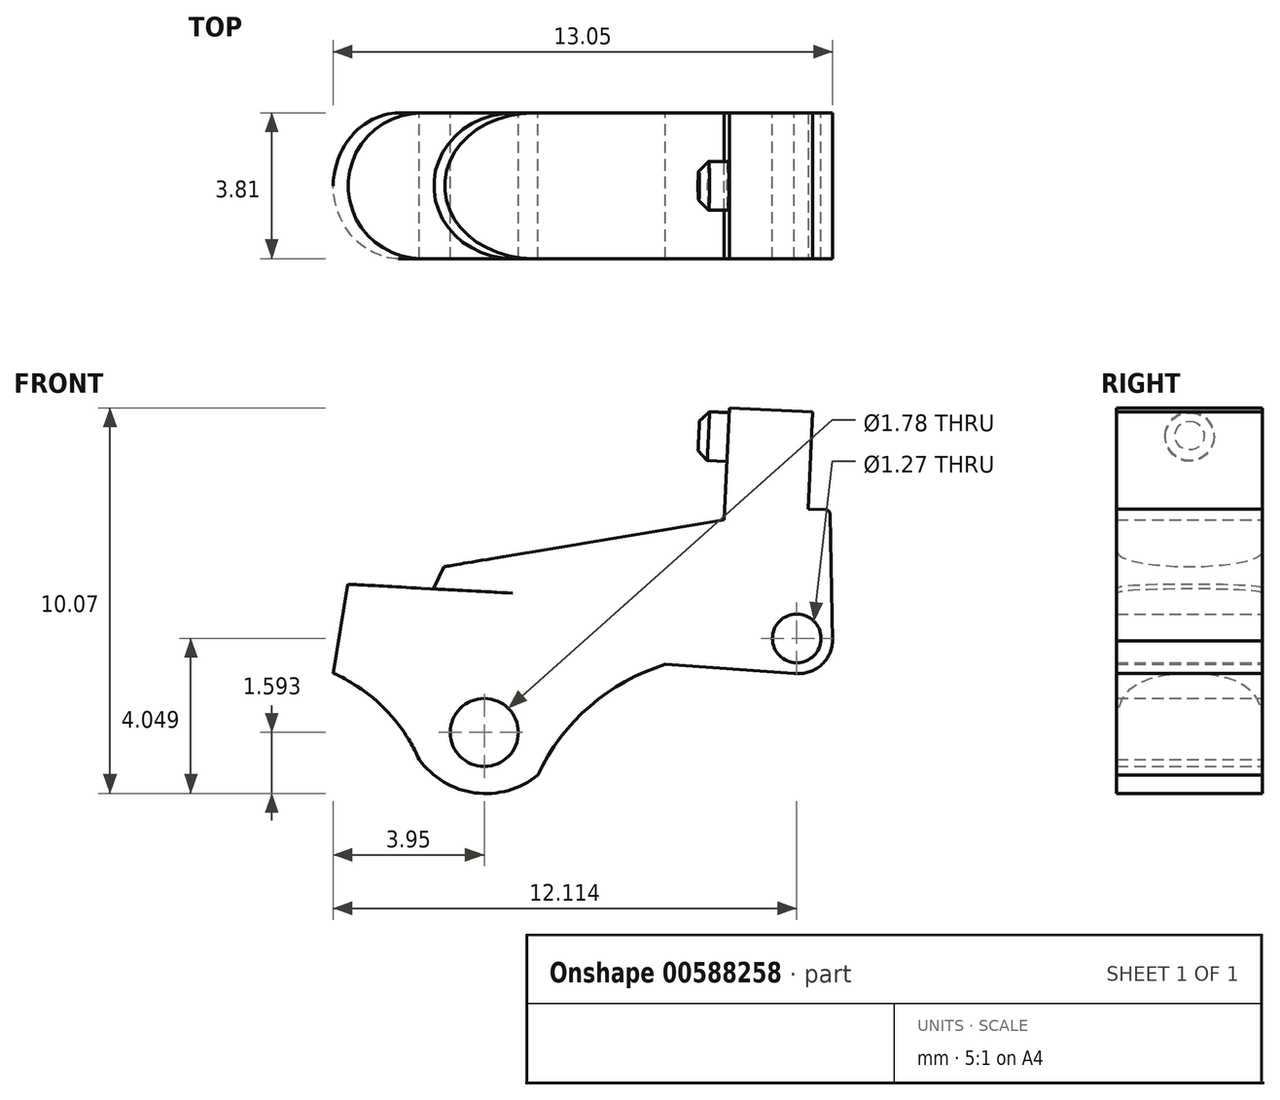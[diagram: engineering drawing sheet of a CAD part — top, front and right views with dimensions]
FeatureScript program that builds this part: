
annotation { "Feature Type Name" : "Feature", "Feature Type Description" : "" }
export const myFeature = defineFeature(function(context is Context, id is Id, definition is map)
    precondition{}
    {
        {
            var Q0;
            Q0=qCreatedBy(makeId("Front.planeOp"),FACE);
            var sketch = newSketch(context, id + "F0", { "sketchPlane" : qUnion([Q0])});
            skPoint(sketch, "E0.endSnap0", {"position": v(-39.55, 26.31) * mm});
            skLineSegment(sketch, "E1", {"start": v(-42.35, 27.7) * mm, "end": v(-42.32, 27.7) * mm});
            skLineSegment(sketch, "E2", {"start": v(-39.7, 29.9) * mm, "end": v(-39.41, 30.48) * mm});
            skLineSegment(sketch, "E3", {"start": v(-42.32, 27.7) * mm, "end": v(-41.93, 30.03) * mm});
            skLineSegment(sketch, "E4", {"start": v(-41.93, 30.03) * mm, "end": v(-39.7, 29.9) * mm});
            skArc(sketch, "E5", {"start": v(-33.64, 27.93) * mm, "mid": v(-35.61, 26.84) * mm, "end": v(-36.97, 25.04) * mm});
            skArc(sketch, "E6", {"start": v(-40.07, 25.45) * mm, "mid": v(-38.61, 24.58) * mm, "end": v(-36.97, 25.04) * mm});
            skArc(sketch, "E7", {"start": v(-40.07, 25.45) * mm, "mid": v(-40.98, 26.79) * mm, "end": v(-42.32, 27.7) * mm});
            skPoint(sketch, "E8", {"position": v(-38.37, 26.15) * mm});
            skPoint(sketch, "E9", {"position": v(-30.2, 28.6) * mm});
            skArc(sketch, "E10", {"start": v(-30.27, 27.7) * mm, "mid": v(-29.58, 27.9) * mm, "end": v(-29.27, 28.54) * mm});
            skLineSegment(sketch, "E11", {"start": v(-33.64, 27.93) * mm, "end": v(-30.27, 27.7) * mm});
            skLineSegment(sketch, "E12", {"start": v(-29.34, 31.97) * mm, "end": v(-29.27, 28.54) * mm});
            skLineSegment(sketch, "E13", {"start": v(-29.93, 31.98) * mm, "end": v(-29.34, 31.97) * mm});
            skLineSegment(sketch, "E14", {"start": v(-32.1, 31.7) * mm, "end": v(-39.41, 30.48) * mm});
            skLineSegment(sketch, "E15", {"start": v(-32.1, 31.7) * mm, "end": v(-29.93, 31.6) * mm});
            skLineSegment(sketch, "E16", {"start": v(-29.93, 31.6) * mm, "end": v(-29.93, 31.98) * mm});
            skSolve(sketch);
        }
        {
            var Q0;
            Q0=makeQuery(id+"F0.imprint","IMPRINT",FACE,{"disambiguationData":[TD([[makeQuery(id+"F0.imprint","IMPRINT",EDGE,{"derivedFrom":sQuery(id+"F0.wireOp",EDGE,"XtgpBi29-hZdu-IJ4v-2hRb-GrWAqEsHX9dT")}),1.0]])]});
            var Q1;
            Q1=makeQuery(id+"F0.imprint","IMPRINT",FACE,{"disambiguationData":[TD([[makeQuery(id+"F0.imprint","IMPRINT",EDGE,{"derivedFrom":sQuery(id+"F0.wireOp",EDGE,"SH1BlDCy-ben9-7Bih-QEMJ-hkyp0oMKCMqf")}),-1.0]])]});
            var Q2;
            Q2=makeQuery(id+"F0.imprint","IMPRINT",FACE,{"disambiguationData":[TD([[makeQuery(id+"F0.imprint","IMPRINT",EDGE,{"derivedFrom":sQuery(id+"F0.wireOp",EDGE,"4IQ7uCOf-OpRu-oNOt-Ximv-gZxlPO9EdMKe")}),-1.0]])]});
            var Q3;
            Q3=makeQuery(id+"F0.imprint","IMPRINT",FACE,{"disambiguationData":[TD([[makeQuery(id+"F0.imprint","IMPRINT",EDGE,{"derivedFrom":sQuery(id+"F0.wireOp",EDGE,"1zMJskkY-9JtC-wsuj-hyEu-qVcM1r3W9rE8")}),-1.0]])]});
            var Q4;
            Q4=makeQuery(id+"F0.imprint","IMPRINT",FACE,{"disambiguationData":[TD([[makeQuery(id+"F0.imprint","IMPRINT",EDGE,{"derivedFrom":sQuery(id+"F0.wireOp",EDGE,"l1qFyu6v-S8hr-JUfp-RZRq-tv3ZL00Pbxo8")}),-1.0]])]});
            var Q5;
            Q5=makeQuery(id+"F0.imprint","IMPRINT",FACE,{"disambiguationData":[TD([[makeQuery(id+"F0.imprint","IMPRINT",EDGE,{"derivedFrom":sQuery(id+"F0.wireOp",EDGE,"E2")}),-1.0]])]});
            extrude(context, id + "F1", {"entities" : qUnion([Q0, Q1, Q2, Q3, Q4, Q5]), "depth" : 3.8 * mm, "offsetDistance" : 25.4 * mm});
        }
        {
            var Q0;
            Q0=sQuery(id+"F0.wireOp",VERTEX,"E8");
            var Q1;
            Q1=makeQuery(id+"F1.opExtrude","SWEPT_BODY",BODY,{"disambiguationData":[OSD([sQuery(id+"F0.wireOp",EDGE,"1zMJskkY-9JtC-wsuj-hyEu-qVcM1r3W9rE8"),sQuery(id+"F0.wireOp",EDGE,"l1qFyu6v-S8hr-JUfp-RZRq-tv3ZL00Pbxo8"),sQuery(id+"F0.wireOp",EDGE,"DFzDxVhI-jG55-MAww-IJIK-aGA0GY1q9XIu"),sQuery(id+"F0.wireOp",EDGE,"2sjn4KcF-YHEf-rL5s-vi8B-RyyOeaxu2GJH"),sQuery(id+"F0.wireOp",EDGE,"ZRnhoPJo-s9wS-XhJK-mMub-YyfMsIm0WNS7"),sQuery(id+"F0.wireOp",EDGE,"RaqrJPhY-hEFq-ETqe-Oz3C-N2TFizCfCjeA"),sQuery(id+"F0.wireOp",EDGE,"3xQdwFbX-rFU0-QzM3-xSzQ-lxiFOViieV5f"),sQuery(id+"F0.wireOp",EDGE,"QoBbz4Ri-XYGi-c3Cy-dZP1-2zNAlRZId6Fp"),sQuery(id+"F0.wireOp",EDGE,"E2"),sQuery(id+"F0.wireOp",EDGE,"EIJsCXqH-8QnJ-VyKu-zHTw-Jm5wh79mehWy"),sQuery(id+"F0.wireOp",EDGE,"E3"),sQuery(id+"F0.wireOp",EDGE,"E4"),sQuery(id+"F0.wireOp",EDGE,"E5"),sQuery(id+"F0.wireOp",EDGE,"E6"),sQuery(id+"F0.wireOp",EDGE,"E7")])]});
            hole(context, id + "F2", {"style" : HoleStyle.SIMPLE, "endStyle" : HoleEndStyle.THROUGH, "oppositeDirection" : true, "holeDiameter" : 1.78 * mm, "majorDiameter" : 6.35 * mm, "isTappedThrough" : true, "tappedDepth" : 12.7 * mm, "tapClearance" : 3, "locations" : qUnion([Q0]), "scope" : qUnion([Q1])});
        }
        {
            var Q0;
            Q0=sQuery(id+"F0.wireOp",VERTEX,"E9");
            var Q1;
            Q1=makeQuery(id+"F1.opExtrude","SWEPT_BODY",BODY,{"disambiguationData":[OSD([sQuery(id+"F0.wireOp",EDGE,"1zMJskkY-9JtC-wsuj-hyEu-qVcM1r3W9rE8"),sQuery(id+"F0.wireOp",EDGE,"l1qFyu6v-S8hr-JUfp-RZRq-tv3ZL00Pbxo8"),sQuery(id+"F0.wireOp",EDGE,"DFzDxVhI-jG55-MAww-IJIK-aGA0GY1q9XIu"),sQuery(id+"F0.wireOp",EDGE,"2sjn4KcF-YHEf-rL5s-vi8B-RyyOeaxu2GJH"),sQuery(id+"F0.wireOp",EDGE,"ZRnhoPJo-s9wS-XhJK-mMub-YyfMsIm0WNS7"),sQuery(id+"F0.wireOp",EDGE,"RaqrJPhY-hEFq-ETqe-Oz3C-N2TFizCfCjeA"),sQuery(id+"F0.wireOp",EDGE,"3xQdwFbX-rFU0-QzM3-xSzQ-lxiFOViieV5f"),sQuery(id+"F0.wireOp",EDGE,"QoBbz4Ri-XYGi-c3Cy-dZP1-2zNAlRZId6Fp"),sQuery(id+"F0.wireOp",EDGE,"E2"),sQuery(id+"F0.wireOp",EDGE,"EIJsCXqH-8QnJ-VyKu-zHTw-Jm5wh79mehWy"),sQuery(id+"F0.wireOp",EDGE,"E3"),sQuery(id+"F0.wireOp",EDGE,"E4"),sQuery(id+"F0.wireOp",EDGE,"E5"),sQuery(id+"F0.wireOp",EDGE,"E6"),sQuery(id+"F0.wireOp",EDGE,"E7")])]});
            hole(context, id + "F3", {"style" : HoleStyle.SIMPLE, "endStyle" : HoleEndStyle.THROUGH, "oppositeDirection" : true, "holeDiameter" : 1.27 * mm, "majorDiameter" : 6.35 * mm, "isTappedThrough" : true, "tappedDepth" : 12.7 * mm, "tapClearance" : 3, "locations" : qUnion([Q0]), "scope" : qUnion([Q1])});
        }
        {
            var Q0;
            Q0=makeQuery(id+"F1.opExtrude","CAP_EDGE",EDGE,{"disambiguationData":[OSD([sQuery(id+"F0.wireOp",EDGE,"E3")])],"isStart":false});
            var Q1;
            Q1=makeQuery(id+"F1.opExtrude","CAP_EDGE",EDGE,{"disambiguationData":[OSD([sQuery(id+"F0.wireOp",EDGE,"E3")])],"isStart":true});
            var Q2;
            Q2=makeQuery(id+"F1.opExtrude","CAP_EDGE",EDGE,{"disambiguationData":[OSD([sQuery(id+"F0.wireOp",EDGE,"E2")])],"isStart":false});
            var Q3;
            Q3=makeQuery(id+"F1.opExtrude","CAP_EDGE",EDGE,{"disambiguationData":[OSD([sQuery(id+"F0.wireOp",EDGE,"E2")])],"isStart":true});
            fillet(context, id + "F4", {"entities" : qUnion([Q0, Q1, Q2, Q3]), "radius" : 1.9 * mm, "tangentPropagation" : true, "allowEdgeOverflow" : false});
        }
        {
            var Q0;
            Q0=makeQuery(id+"F1.opExtrude","SWEPT_FACE",FACE,{"disambiguationData":[OSD([sQuery(id+"F0.wireOp",EDGE,"nkTQsHem-Ju75-uTIL-WYU6-FnTE0oEh7rBz")])]});
            var Q1;
            Q1=makeQuery(id+"F1.opExtrude","SWEPT_FACE",FACE,{"disambiguationData":[OSD([sQuery(id+"F0.wireOp",EDGE,"E15")])]});
            extrude(context, id + "F5", {"entities" : qUnion([Q0, Q1]), "operationType" : NewBodyOperationType.ADD, "depth" : 2.92 * mm, "offsetDistance" : 25.4 * mm});
        }
        {
            var Q0;
            Q0=makeQuery(id+"F5.opExtrude","SWEPT_FACE",FACE,{"disambiguationData":[OSD([sQuery(id+"F0.wireOp",EDGE,"E14"),sQuery(id+"F0.wireOp",EDGE,"E15")])]});
            var sketch = newSketch(context, id + "F6", { "sketchPlane" : qUnion([Q0])});
            skPoint(sketch, "E17.positionSnap0", {"position": v(1.9, 33.08) * mm});
            skPoint(sketch, "E17.positionSnap1", {"position": v(0, 31.62) * mm});
            skCircle(sketch, "E18", {"center": v(1.9, 32.33) * mm, "radius": 0.64 * mm});
            skSolve(sketch);
        }
        {
            var Q0;
            Q0=makeQuery(id+"F6.imprint","IMPRINT",FACE,{"disambiguationData":[TD([[makeQuery(id+"F6.imprint","IMPRINT",EDGE,{"derivedFrom":sQuery(id+"F6.wireOp",EDGE,"qL4xBT2M-Zw5A-9IWh-TJ8F-d7QDiRx62KFr")}),1.0]])]});
            var Q1;
            Q1=makeQuery(id+"F6.imprint","IMPRINT",FACE,{"disambiguationData":[TD([[makeQuery(id+"F6.imprint","IMPRINT",EDGE,{"derivedFrom":sQuery(id+"F6.wireOp",EDGE,"XZjglXE4-oGhE-HlDz-rg4o-eZbCbJht96xO")}),1.0]])]});
            var Q2;
            Q2=makeQuery(id+"F6.imprint","IMPRINT",FACE,{"disambiguationData":[TD([[makeQuery(id+"F6.imprint","IMPRINT",EDGE,{"derivedFrom":sQuery(id+"F6.wireOp",EDGE,"E18")}),1.0]])]});
            extrude(context, id + "F7", {"entities" : qUnion([Q0, Q1, Q2]), "operationType" : NewBodyOperationType.ADD, "depth" : 0.76 * mm, "offsetDistance" : 25.4 * mm});
        }
        {
            var Q0;
            Q0=makeQuery(id+"F7.opExtrude","CAP_EDGE",EDGE,{"disambiguationData":[OSD([sQuery(id+"F6.wireOp",EDGE,"E18")])],"isStart":false});
            chamfer(context, id + "F8", {"entities" : qUnion([Q0]), "width" : 0.25 * mm, "tangentPropagation" : true});
        }
        {
            var Q0;
            Q0=makeQuery(id+"F1.opExtrude","SWEPT_EDGE",EDGE,{"disambiguationData":[OSD([sQuery(id+"F0.wireOp",EDGE,"E12"),sQuery(id+"F0.wireOp",EDGE,"E13")])]});
            fillet(context, id + "F9", {"entities" : qUnion([Q0]), "radius" : 0.13 * mm, "tangentPropagation" : true, "allowEdgeOverflow" : false});
        }
    });
